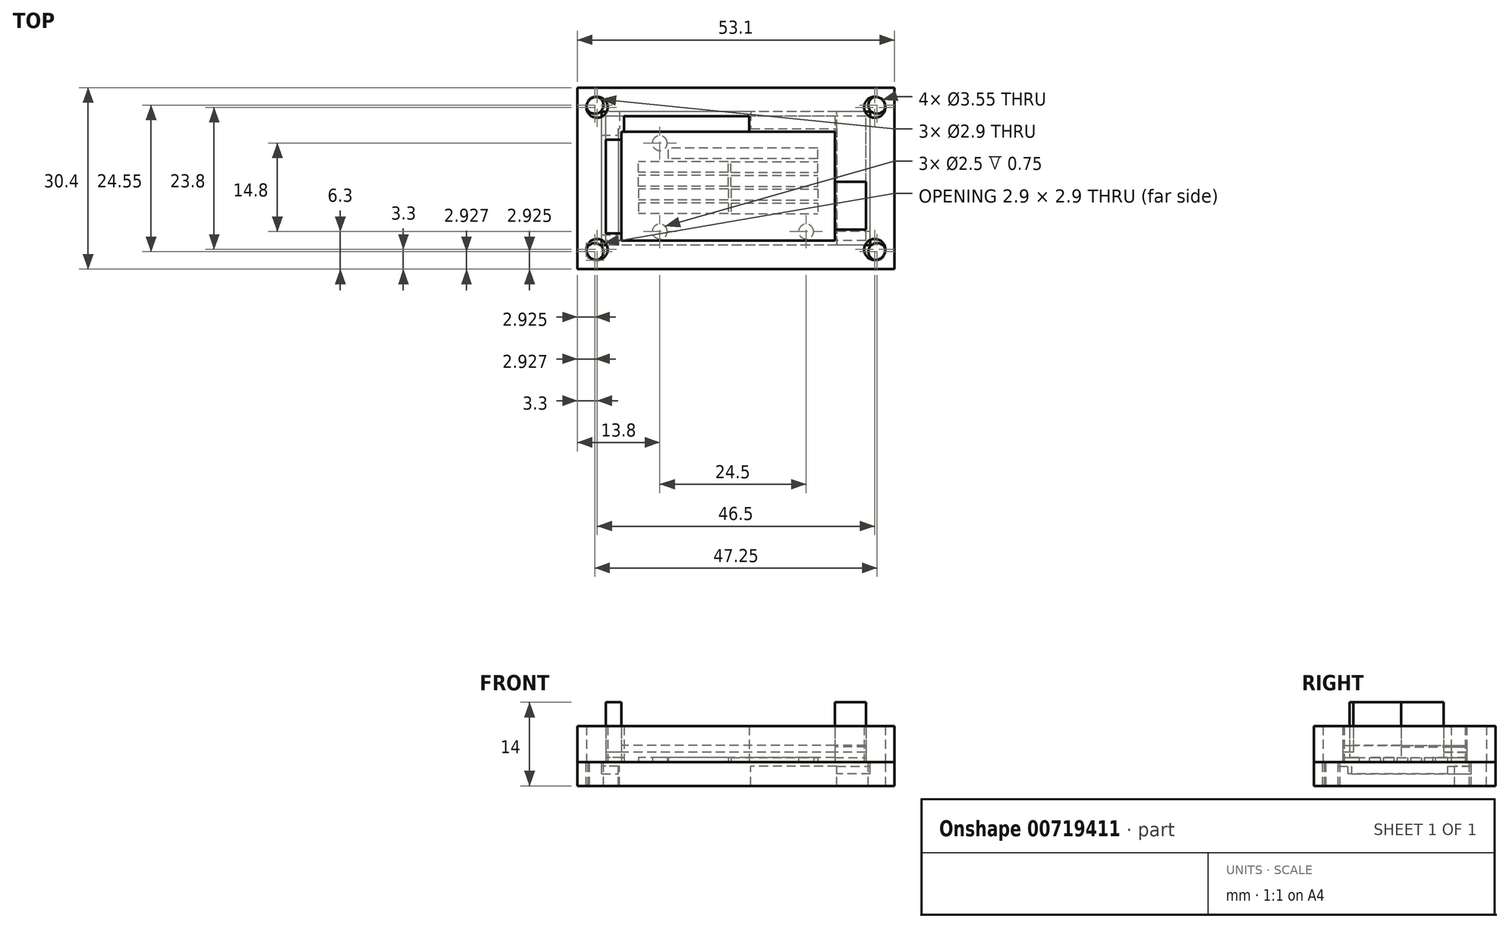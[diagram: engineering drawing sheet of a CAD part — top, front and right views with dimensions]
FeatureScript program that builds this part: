
annotation { "Feature Type Name" : "Feature", "Feature Type Description" : "" }
export const myFeature = defineFeature(function(context is Context, id is Id, definition is map)
    precondition{}
    {
        {
            var Q0;
            Q0=qCreatedBy(makeId("Top.planeOp"),FACE);
            var sketch = newSketch(context, id + "F0", { "sketchPlane" : qUnion([Q0])});
            skLineSegment(sketch, "E0.bottom", {"start": v(21.75, -10.4) * mm, "end": v(-21.75, -10.4) * mm});
            skLineSegment(sketch, "E0.top", {"start": v(21.75, 10.4) * mm, "end": v(-21.75, 10.4) * mm});
            skLineSegment(sketch, "E0.left", {"start": v(21.75, -10.4) * mm, "end": v(21.75, 10.4) * mm});
            skLineSegment(sketch, "E0.right", {"start": v(-21.75, -10.4) * mm, "end": v(-21.75, 10.4) * mm});
            skPoint(sketch, "E0.middle", {"position": v(0, 0) * mm});
            skLineSegment(sketch, "E1.bottom", {"start": v(-21.75, 6.5) * mm, "end": v(-19.15, 6.5) * mm});
            skLineSegment(sketch, "E1.top", {"start": v(-21.75, -9.2) * mm, "end": v(-19.15, -9.2) * mm});
            skLineSegment(sketch, "E1.left", {"start": v(-21.75, 6.5) * mm, "end": v(-21.75, -9.2) * mm});
            skLineSegment(sketch, "E1.right", {"start": v(-19.15, 6.5) * mm, "end": v(-19.15, -9.2) * mm});
            skLineSegment(sketch, "E2.bottom", {"start": v(-18.75, 10.4) * mm, "end": v(2.25, 10.4) * mm});
            skLineSegment(sketch, "E2.top", {"start": v(-18.75, 7.8) * mm, "end": v(2.25, 7.8) * mm});
            skLineSegment(sketch, "E2.left", {"start": v(-18.75, 10.4) * mm, "end": v(-18.75, 7.8) * mm});
            skLineSegment(sketch, "E2.right", {"start": v(2.25, 10.4) * mm, "end": v(2.25, 7.8) * mm});
            skLineSegment(sketch, "E3.bottom", {"start": v(21.75, -0.6) * mm, "end": v(16.55, -0.6) * mm});
            skLineSegment(sketch, "E3.top", {"start": v(21.75, -8.6) * mm, "end": v(16.55, -8.6) * mm});
            skLineSegment(sketch, "E3.left", {"start": v(21.75, -0.6) * mm, "end": v(21.75, -8.6) * mm});
            skLineSegment(sketch, "E3.right", {"start": v(16.55, -0.6) * mm, "end": v(16.55, -8.6) * mm});
            skCircle(sketch, "E4", {"center": v(-12.75, 5.9) * mm, "radius": 1.25 * mm});
            skCircle(sketch, "E5", {"center": v(-12.75, -8.9) * mm, "radius": 1.25 * mm});
            skCircle(sketch, "E6", {"center": v(11.75, -8.9) * mm, "radius": 1.25 * mm});
            skLineSegment(sketch, "E7.bottom", {"start": v(-19.15, -10.4) * mm, "end": v(16.55, -10.4) * mm});
            skLineSegment(sketch, "E7.top", {"start": v(-19.15, 7.8) * mm, "end": v(16.55, 7.8) * mm});
            skLineSegment(sketch, "E7.left", {"start": v(-19.15, -10.4) * mm, "end": v(-19.15, 7.8) * mm});
            skLineSegment(sketch, "E7.right", {"start": v(16.55, -10.4) * mm, "end": v(16.55, 7.8) * mm});
            skLineSegment(sketch, "E8.top", {"start": v(21.75, 10.4) * mm, "end": v(16.55, 10.4) * mm});
            skLineSegment(sketch, "E8.left", {"start": v(21.75, -0.6) * mm, "end": v(21.75, 10.4) * mm});
            skLineSegment(sketch, "E8.right", {"start": v(16.55, -0.6) * mm, "end": v(16.55, 10.4) * mm});
            skSolve(sketch);
        }
        {
            var Q0;
            Q0 = qSketchRegion(id + "F0", true);
            var Q1;
            Q1=makeQuery(id+"F0.imprint","IMPRINT",FACE,{"disambiguationData":[TD([[makeQuery(id+"F0.imprint","IMPRINT",EDGE,{"derivedFrom":sQuery(id+"F0.wireOp",EDGE,"E6")}),1.0]])]});
            var Q2;
            Q2=makeQuery(id+"F0.imprint","IMPRINT",FACE,{"disambiguationData":[TD([[makeQuery(id+"F0.imprint","IMPRINT",EDGE,{"derivedFrom":sQuery(id+"F0.wireOp",EDGE,"E5")}),1.0]])]});
            var Q3;
            Q3=makeQuery(id+"F0.imprint","IMPRINT",FACE,{"disambiguationData":[TD([[makeQuery(id+"F0.imprint","IMPRINT",EDGE,{"derivedFrom":sQuery(id+"F0.wireOp",EDGE,"E4")}),1.0]])]});
            extrude(context, id + "F1", {"entities" : qUnion([Q0, Q1, Q2, Q3]), "depth" : 1.6 * mm, "offsetDistance" : 25 * mm});
        }
        {
            var Q0;
            {var subQ0=sQuery(id+"F0.wireOp",EDGE,"E1.bottom");Q0=makeQuery(id+"F0.imprint","IMPRINT",FACE,{"disambiguationData":[TD([[makeQuery(id+"F0.imprint","IMPRINT",EDGE,{"derivedFrom":subQ0}),-1.0]])]});}
            var Q1;
            Q1=makeQuery(id+"F0.imprint","IMPRINT",FACE,{"disambiguationData":[TD([[makeQuery(id+"F0.imprint","IMPRINT",EDGE,{"derivedFrom":sQuery(id+"F0.wireOp",EDGE,"E2.bottom")}),-1.0]])]});
            var Q2;
            {var subQ0=sQuery(id+"F0.wireOp",EDGE,"E3.top");Q2=makeQuery(id+"F0.imprint","IMPRINT",FACE,{"disambiguationData":[TD([[makeQuery(id+"F0.imprint","IMPRINT",EDGE,{"derivedFrom":subQ0}),-1.0]])]});}
            extrude(context, id + "F2", {"entities" : qUnion([Q0, Q1, Q2]), "operationType" : NewBodyOperationType.ADD, "depth" : 10 * mm, "offsetDistance" : 25 * mm});
        }
        {
            var Q0;
            Q0=makeQuery(id+"F0.imprint","IMPRINT",FACE,{"disambiguationData":[TD([[makeQuery(id+"F0.imprint","IMPRINT",EDGE,{"derivedFrom":sQuery(id+"F0.wireOp",EDGE,"E4")}),-1.0]])]});
            var Q1;
            {var subQ2=sQuery(id+"F0.wireOp",EDGE,"E3.bottom");Q1=makeQuery(id+"F0.imprint","IMPRINT",FACE,{"disambiguationData":[TD([[makeQuery(id+"F0.imprint","IMPRINT",EDGE,{"derivedFrom":subQ2}),-1.0]])]});}
            var Q2;
            Q2=makeQuery(id+"F0.imprint","IMPRINT",FACE,{"disambiguationData":[TD([[makeQuery(id+"F0.imprint","IMPRINT",EDGE,{"derivedFrom":sQuery(id+"F0.wireOp",EDGE,"E4")}),1.0]])]});
            var Q3;
            Q3=makeQuery(id+"F0.imprint","IMPRINT",FACE,{"disambiguationData":[TD([[makeQuery(id+"F0.imprint","IMPRINT",EDGE,{"derivedFrom":sQuery(id+"F0.wireOp",EDGE,"E5")}),1.0]])]});
            var Q4;
            Q4=makeQuery(id+"F0.imprint","IMPRINT",FACE,{"disambiguationData":[TD([[makeQuery(id+"F0.imprint","IMPRINT",EDGE,{"derivedFrom":sQuery(id+"F0.wireOp",EDGE,"E6")}),1.0]])]});
            extrude(context, id + "F3", {"entities" : qUnion([Q0, Q1, Q2, Q3, Q4]), "operationType" : NewBodyOperationType.ADD, "depth" : 2.8 * mm, "offsetDistance" : 25 * mm});
        }
        {
            var Q0;
            Q0=qCreatedBy(makeId("Top.planeOp"),FACE);
            var sketch = newSketch(context, id + "F4", { "sketchPlane" : qUnion([Q0])});
            skLineSegment(sketch, "E9.bottom", {"start": v(26.55, -15.2) * mm, "end": v(-26.55, -15.2) * mm});
            skLineSegment(sketch, "E9.top", {"start": v(26.55, 15.2) * mm, "end": v(-26.55, 15.2) * mm});
            skLineSegment(sketch, "E9.left", {"start": v(26.55, -15.2) * mm, "end": v(26.55, 15.2) * mm});
            skLineSegment(sketch, "E9.right", {"start": v(-26.55, -15.2) * mm, "end": v(-26.55, 15.2) * mm});
            skPoint(sketch, "E9.middle", {"position": v(0, 0) * mm});
            skLineSegment(sketch, "E10.bottom", {"start": v(24.75, -13.4) * mm, "end": v(-24.75, -13.4) * mm});
            skLineSegment(sketch, "E10.top", {"start": v(24.75, 13.4) * mm, "end": v(-24.75, 13.4) * mm});
            skLineSegment(sketch, "E10.left", {"start": v(24.75, -13.4) * mm, "end": v(24.75, 13.4) * mm});
            skLineSegment(sketch, "E10.right", {"start": v(-24.75, -13.4) * mm, "end": v(-24.75, 13.4) * mm});
            skLineSegment(sketch, "E11.bottom", {"start": v(22.5, -11.15) * mm, "end": v(-22.5, -11.15) * mm});
            skLineSegment(sketch, "E11.top", {"start": v(22.5, 11.15) * mm, "end": v(-22.5, 11.15) * mm});
            skLineSegment(sketch, "E11.left", {"start": v(22.5, -11.15) * mm, "end": v(22.5, 11.15) * mm});
            skLineSegment(sketch, "E11.right", {"start": v(-22.5, -11.15) * mm, "end": v(-22.5, 11.15) * mm});
            skLineSegment(sketch, "E12.bottom", {"start": v(-22.5, 7.25) * mm, "end": v(-19.7, 7.25) * mm});
            skLineSegment(sketch, "E12.top", {"start": v(-22.5, -9.45) * mm, "end": v(-19.7, -9.45) * mm});
            skLineSegment(sketch, "E12.left", {"start": v(-22.5, 7.25) * mm, "end": v(-22.5, -9.45) * mm});
            skLineSegment(sketch, "E12.right", {"start": v(-19.7, 7.25) * mm, "end": v(-19.7, -9.45) * mm});
            skLineSegment(sketch, "E13.bottom", {"start": v(-19.5, 11.15) * mm, "end": v(2.5, 11.15) * mm});
            skLineSegment(sketch, "E13.top", {"start": v(-19.5, 8.35) * mm, "end": v(2.5, 8.35) * mm});
            skLineSegment(sketch, "E13.left", {"start": v(-19.5, 11.15) * mm, "end": v(-19.5, 8.35) * mm});
            skLineSegment(sketch, "E13.right", {"start": v(2.5, 11.15) * mm, "end": v(2.5, 8.35) * mm});
            skLineSegment(sketch, "E14.bottom", {"start": v(22.5, 0.15) * mm, "end": v(16.9, 0.15) * mm});
            skLineSegment(sketch, "E14.top", {"start": v(22.5, -8.85) * mm, "end": v(16.9, -8.85) * mm});
            skLineSegment(sketch, "E14.left", {"start": v(22.5, 0.15) * mm, "end": v(22.5, -8.85) * mm});
            skLineSegment(sketch, "E14.right", {"start": v(16.9, 0.15) * mm, "end": v(16.9, -8.85) * mm});
            skLineSegment(sketch, "E15.bottom", {"start": v(-19.7, -11.15) * mm, "end": v(16.9, -11.15) * mm});
            skLineSegment(sketch, "E15.top", {"start": v(-19.7, 8.35) * mm, "end": v(16.9, 8.35) * mm});
            skLineSegment(sketch, "E15.left", {"start": v(-19.7, -11.15) * mm, "end": v(-19.7, 8.35) * mm});
            skLineSegment(sketch, "E15.right", {"start": v(16.9, -11.15) * mm, "end": v(16.9, 8.35) * mm});
            skLineSegment(sketch, "E16.top", {"start": v(22.5, 11.15) * mm, "end": v(16.9, 11.15) * mm});
            skLineSegment(sketch, "E16.left", {"start": v(22.5, 0.15) * mm, "end": v(22.5, 11.15) * mm});
            skLineSegment(sketch, "E16.right", {"start": v(16.9, 0.15) * mm, "end": v(16.9, 11.15) * mm});
            skLineSegment(sketch, "E17", {"start": v(-22.5, 11.15) * mm, "end": v(-24.75, 13.4) * mm, "construction": true});
            skCircle(sketch, "E18", {"center": v(-23.62, 12.27) * mm, "radius": 1.45 * mm});
            skCircle(sketch, "E19", {"center": v(-23.62, 12.27) * mm, "radius": 3 * mm, "construction": true});
            skLineSegment(sketch, "E20", {"start": v(-22.5, -11.15) * mm, "end": v(-24.75, -13.4) * mm, "construction": true});
            skLineSegment(sketch, "E21", {"start": v(22.5, -11.15) * mm, "end": v(24.75, -13.4) * mm, "construction": true});
            skLineSegment(sketch, "E22", {"start": v(22.5, 11.15) * mm, "end": v(24.75, 13.4) * mm, "construction": true});
            skCircle(sketch, "E23", {"center": v(23.62, 12.28) * mm, "radius": 1.45 * mm});
            skCircle(sketch, "E24", {"center": v(23.62, -12.28) * mm, "radius": 1.45 * mm});
            skCircle(sketch, "E25", {"center": v(-23.63, -12.27) * mm, "radius": 1.45 * mm});
            skSolve(sketch);
        }
        {
            var Q0;
            {var subQ0=sQuery(id+"F4.wireOp",EDGE,"E10.left");var subQ1=sQuery(id+"F4.wireOp",EDGE,"E10.bottom");var subQ2=makeQuery(id+"F4.imprint","INTERSECT",VERTEX,{"derivedFrom":[subQ1,subQ0]});Q0=makeQuery(id+"F4.imprint","IMPRINT",FACE,{"disambiguationData":[TD([[makeQuery(id+"F4.imprint","IMPRINT",EDGE,{"disambiguationData":[TD([[subQ2,-1.0]])],"derivedFrom":subQ1}),-1.0]])]});}
            var Q1;
            Q1=makeQuery(id+"F4.imprint","IMPRINT",FACE,{"disambiguationData":[TD([[makeQuery(id+"F4.imprint","IMPRINT",EDGE,{"derivedFrom":sQuery(id+"F4.wireOp",EDGE,"E9.bottom")}),-1.0]])]});
            var Q2;
            {var subQ0=sQuery(id+"F4.wireOp",EDGE,"E14.top");Q2=makeQuery(id+"F4.imprint","IMPRINT",FACE,{"disambiguationData":[TD([[makeQuery(id+"F4.imprint","IMPRINT",EDGE,{"derivedFrom":subQ0}),-1.0]])]});}
            var Q3;
            {var subQ2=sQuery(id+"F4.wireOp",EDGE,"E14.bottom");Q3=makeQuery(id+"F4.imprint","IMPRINT",FACE,{"disambiguationData":[TD([[makeQuery(id+"F4.imprint","IMPRINT",EDGE,{"derivedFrom":subQ2}),-1.0]])]});}
            var Q4;
            Q4=makeQuery(id+"F4.imprint","IMPRINT",FACE,{"disambiguationData":[TD([[makeQuery(id+"F4.imprint","IMPRINT",EDGE,{"derivedFrom":sQuery(id+"F4.wireOp",EDGE,"E13.bottom")}),-1.0]])]});
            var Q5;
            {var subQ0=sQuery(id+"F4.wireOp",EDGE,"E12.bottom");Q5=makeQuery(id+"F4.imprint","IMPRINT",FACE,{"disambiguationData":[TD([[makeQuery(id+"F4.imprint","IMPRINT",EDGE,{"derivedFrom":subQ0}),-1.0]])]});}
            var Q6;
            {var subQ0=sQuery(id+"F4.wireOp",EDGE,"E12.bottom");Q6=makeQuery(id+"F4.imprint","IMPRINT",FACE,{"disambiguationData":[TD([[makeQuery(id+"F4.imprint","IMPRINT",EDGE,{"derivedFrom":subQ0}),1.0]])]});}
            var Q7;
            {var subQ3=sQuery(id+"F4.wireOp",EDGE,"E13.right");Q7=makeQuery(id+"F4.imprint","IMPRINT",FACE,{"disambiguationData":[TD([[makeQuery(id+"F4.imprint","IMPRINT",EDGE,{"derivedFrom":subQ3}),1.0]])]});}
            var Q8;
            {var subQ5=sQuery(id+"F4.wireOp",EDGE,"E12.top");Q8=makeQuery(id+"F4.imprint","IMPRINT",FACE,{"disambiguationData":[TD([[makeQuery(id+"F4.imprint","IMPRINT",EDGE,{"derivedFrom":subQ5}),-1.0]])]});}
            var Q9;
            {var subQ0=sQuery(id+"F4.wireOp",EDGE,"E11.left");Q9=makeQuery(id+"F4.imprint","IMPRINT",FACE,{"disambiguationData":[TD([[makeQuery(id+"F4.imprint","IMPRINT",EDGE,{"derivedFrom":subQ0}),1.0]])]});}
            var Q10;
            {var subQ9=sQuery(id+"F4.wireOp",EDGE,"E15.bottom");Q10=makeQuery(id+"F4.imprint","IMPRINT",FACE,{"disambiguationData":[TD([[makeQuery(id+"F4.imprint","IMPRINT",EDGE,{"derivedFrom":subQ9}),1.0]])]});}
            var Q11;
            {var subQ13=sQuery(id+"F4.wireOp",EDGE,"E11.left");Q11=makeQuery(id+"F4.imprint","IMPRINT",FACE,{"disambiguationData":[TD([[makeQuery(id+"F4.imprint","IMPRINT",EDGE,{"derivedFrom":subQ13}),-1.0]])]});}
            var Q12;
            {var subQ0=sQuery(id+"F4.wireOp",EDGE,"E10.left");var subQ1=sQuery(id+"F4.wireOp",EDGE,"E10.top");var subQ2=makeQuery(id+"F4.imprint","INTERSECT",VERTEX,{"derivedFrom":[subQ1,subQ0]});Q12=makeQuery(id+"F4.imprint","IMPRINT",FACE,{"disambiguationData":[TD([[makeQuery(id+"F4.imprint","IMPRINT",EDGE,{"disambiguationData":[TD([[subQ2,-1.0]])],"derivedFrom":subQ1}),1.0]])]});}
            var Q13;
            {var subQ0=sQuery(id+"F4.wireOp",EDGE,"E10.right");var subQ1=sQuery(id+"F4.wireOp",EDGE,"E10.top");var subQ2=makeQuery(id+"F4.imprint","INTERSECT",VERTEX,{"derivedFrom":[subQ1,subQ0]});Q13=makeQuery(id+"F4.imprint","IMPRINT",FACE,{"disambiguationData":[TD([[makeQuery(id+"F4.imprint","IMPRINT",EDGE,{"disambiguationData":[TD([[subQ2,1.0]])],"derivedFrom":subQ1}),1.0]])]});}
            extrude(context, id + "F5", {"entities" : qUnion([Q0, Q1, Q2, Q3, Q4, Q5, Q6, Q7, Q8, Q9, Q10, Q11, Q12, Q13]), "oppositeDirection" : true, "depth" : 4 * mm, "offsetDistance" : 25 * mm});
        }
        {
            var Q0;
            Q0=makeQuery(id+"F4.imprint","IMPRINT",FACE,{"disambiguationData":[TD([[makeQuery(id+"F4.imprint","IMPRINT",EDGE,{"derivedFrom":sQuery(id+"F4.wireOp",EDGE,"E13.bottom")}),-1.0]])]});
            var Q1;
            {var subQ9=sQuery(id+"F4.wireOp",EDGE,"E15.bottom");Q1=makeQuery(id+"F4.imprint","IMPRINT",FACE,{"disambiguationData":[TD([[makeQuery(id+"F4.imprint","IMPRINT",EDGE,{"derivedFrom":subQ9}),1.0]])]});}
            var Q2;
            {var subQ0=sQuery(id+"F4.wireOp",EDGE,"E12.bottom");Q2=makeQuery(id+"F4.imprint","IMPRINT",FACE,{"disambiguationData":[TD([[makeQuery(id+"F4.imprint","IMPRINT",EDGE,{"derivedFrom":subQ0}),-1.0]])]});}
            var Q3;
            {var subQ2=sQuery(id+"F4.wireOp",EDGE,"E14.bottom");Q3=makeQuery(id+"F4.imprint","IMPRINT",FACE,{"disambiguationData":[TD([[makeQuery(id+"F4.imprint","IMPRINT",EDGE,{"derivedFrom":subQ2}),-1.0]])]});}
            var Q4;
            {var subQ0=sQuery(id+"F4.wireOp",EDGE,"E14.top");Q4=makeQuery(id+"F4.imprint","IMPRINT",FACE,{"disambiguationData":[TD([[makeQuery(id+"F4.imprint","IMPRINT",EDGE,{"derivedFrom":subQ0}),-1.0]])]});}
            extrude(context, id + "F6", {"entities" : qUnion([Q0, Q1, Q2, Q3, Q4]), "operationType" : NewBodyOperationType.REMOVE, "oppositeDirection" : true, "depth" : 2 * mm, "offsetDistance" : 25 * mm});
        }
        {
            var Q0;
            {var subQ0=sQuery(id+"F4.wireOp",EDGE,"E12.bottom");Q0=makeQuery(id+"F4.imprint","IMPRINT",FACE,{"disambiguationData":[TD([[makeQuery(id+"F4.imprint","IMPRINT",EDGE,{"derivedFrom":subQ0}),1.0]])]});}
            var Q1;
            {var subQ5=sQuery(id+"F4.wireOp",EDGE,"E12.top");Q1=makeQuery(id+"F4.imprint","IMPRINT",FACE,{"disambiguationData":[TD([[makeQuery(id+"F4.imprint","IMPRINT",EDGE,{"derivedFrom":subQ5}),-1.0]])]});}
            var Q2;
            {var subQ0=sQuery(id+"F4.wireOp",EDGE,"E11.left");Q2=makeQuery(id+"F4.imprint","IMPRINT",FACE,{"disambiguationData":[TD([[makeQuery(id+"F4.imprint","IMPRINT",EDGE,{"derivedFrom":subQ0}),1.0]])]});}
            var Q3;
            {var subQ3=sQuery(id+"F4.wireOp",EDGE,"E13.right");Q3=makeQuery(id+"F4.imprint","IMPRINT",FACE,{"disambiguationData":[TD([[makeQuery(id+"F4.imprint","IMPRINT",EDGE,{"derivedFrom":subQ3}),1.0]])]});}
            extrude(context, id + "F7", {"entities" : qUnion([Q0, Q1, Q2, Q3]), "operationType" : NewBodyOperationType.REMOVE, "oppositeDirection" : true, "depth" : 0.75 * mm, "offsetDistance" : 25 * mm});
        }
        {
            var Q0;
            Q0=qCreatedBy(makeId("Top.planeOp"),FACE);
            var sketch = newSketch(context, id + "F8", { "sketchPlane" : qUnion([Q0])});
            skLineSegment(sketch, "E26.bottom", {"start": v(26.55, -15.2) * mm, "end": v(-26.55, -15.2) * mm});
            skLineSegment(sketch, "E26.top", {"start": v(26.55, 15.2) * mm, "end": v(-26.55, 15.2) * mm});
            skLineSegment(sketch, "E26.left", {"start": v(26.55, -15.2) * mm, "end": v(26.55, 15.2) * mm});
            skLineSegment(sketch, "E26.right", {"start": v(-26.55, -15.2) * mm, "end": v(-26.55, 15.2) * mm});
            skLineSegment(sketch, "E27.bottom", {"start": v(24.75, -13.4) * mm, "end": v(-24.75, -13.4) * mm});
            skLineSegment(sketch, "E27.top", {"start": v(24.75, 13.4) * mm, "end": v(-24.75, 13.4) * mm});
            skLineSegment(sketch, "E27.left", {"start": v(24.75, -13.4) * mm, "end": v(24.75, 13.4) * mm});
            skLineSegment(sketch, "E27.right", {"start": v(-24.75, -13.4) * mm, "end": v(-24.75, 13.4) * mm});
            skLineSegment(sketch, "E28.bottom", {"start": v(21.75, -10.4) * mm, "end": v(-21.75, -10.4) * mm});
            skLineSegment(sketch, "E28.top", {"start": v(21.75, 10.4) * mm, "end": v(-21.75, 10.4) * mm});
            skLineSegment(sketch, "E28.left", {"start": v(21.75, -10.4) * mm, "end": v(21.75, 10.4) * mm});
            skLineSegment(sketch, "E28.right", {"start": v(-21.75, -10.4) * mm, "end": v(-21.75, 10.4) * mm});
            skLineSegment(sketch, "E29.bottom", {"start": v(-21.75, 6.5) * mm, "end": v(-19.15, 6.5) * mm});
            skLineSegment(sketch, "E29.top", {"start": v(-21.75, -9.2) * mm, "end": v(-19.15, -9.2) * mm});
            skLineSegment(sketch, "E29.left", {"start": v(-21.75, 6.5) * mm, "end": v(-21.75, -9.2) * mm});
            skLineSegment(sketch, "E29.right", {"start": v(-19.15, 6.5) * mm, "end": v(-19.15, -9.2) * mm});
            skLineSegment(sketch, "E30.bottom", {"start": v(-18.75, 10.4) * mm, "end": v(2.25, 10.4) * mm});
            skLineSegment(sketch, "E30.top", {"start": v(-18.75, 7.8) * mm, "end": v(2.25, 7.8) * mm});
            skLineSegment(sketch, "E30.left", {"start": v(-18.75, 10.4) * mm, "end": v(-18.75, 7.8) * mm});
            skLineSegment(sketch, "E30.right", {"start": v(2.25, 10.4) * mm, "end": v(2.25, 7.8) * mm});
            skLineSegment(sketch, "E31.bottom", {"start": v(21.75, -0.6) * mm, "end": v(16.55, -0.6) * mm});
            skLineSegment(sketch, "E31.top", {"start": v(21.75, -8.6) * mm, "end": v(16.55, -8.6) * mm});
            skLineSegment(sketch, "E31.left", {"start": v(21.75, -0.6) * mm, "end": v(21.75, -8.6) * mm});
            skLineSegment(sketch, "E31.right", {"start": v(16.55, -0.6) * mm, "end": v(16.55, -8.6) * mm});
            skLineSegment(sketch, "E32.bottom", {"start": v(-19.15, -10.4) * mm, "end": v(16.55, -10.4) * mm});
            skLineSegment(sketch, "E32.top", {"start": v(-19.15, 7.8) * mm, "end": v(16.55, 7.8) * mm});
            skLineSegment(sketch, "E32.left", {"start": v(-19.15, -10.4) * mm, "end": v(-19.15, 7.8) * mm});
            skLineSegment(sketch, "E32.right", {"start": v(16.55, -10.4) * mm, "end": v(16.55, 7.8) * mm});
            skLineSegment(sketch, "E33.top", {"start": v(21.75, 10.4) * mm, "end": v(16.55, 10.4) * mm});
            skLineSegment(sketch, "E33.left", {"start": v(21.75, -0.6) * mm, "end": v(21.75, 10.4) * mm});
            skLineSegment(sketch, "E33.right", {"start": v(16.55, -0.6) * mm, "end": v(16.55, 10.4) * mm});
            skLineSegment(sketch, "E34", {"start": v(-21.75, 10.4) * mm, "end": v(-24.75, 13.4) * mm, "construction": true});
            skCircle(sketch, "E35", {"center": v(-23.25, 11.9) * mm, "radius": 1.77 * mm});
            skCircle(sketch, "E36", {"center": v(-23.25, 11.9) * mm, "radius": 3 * mm, "construction": true});
            skLineSegment(sketch, "E37", {"start": v(-21.75, -10.4) * mm, "end": v(-24.75, -13.4) * mm, "construction": true});
            skLineSegment(sketch, "E38", {"start": v(21.75, -10.4) * mm, "end": v(24.75, -13.4) * mm, "construction": true});
            skLineSegment(sketch, "E39", {"start": v(21.75, 10.4) * mm, "end": v(24.75, 13.4) * mm, "construction": true});
            skCircle(sketch, "E40", {"center": v(23.25, 11.9) * mm, "radius": 1.77 * mm});
            skCircle(sketch, "E41", {"center": v(23.25, -11.9) * mm, "radius": 1.77 * mm});
            skCircle(sketch, "E42", {"center": v(-23.25, -11.9) * mm, "radius": 1.77 * mm});
            skCircle(sketch, "E43", {"center": v(-12.75, 5.9) * mm, "radius": 1.25 * mm});
            skCircle(sketch, "E44", {"center": v(-12.75, -8.9) * mm, "radius": 1.25 * mm});
            skCircle(sketch, "E45", {"center": v(11.75, -8.9) * mm, "radius": 1.25 * mm});
            skLineSegment(sketch, "E46", {"start": v(-19.15, -1.3) * mm, "end": v(16.55, -1.3) * mm, "construction": true});
            skLineSegment(sketch, "E47", {"start": v(-1.3, 7.8) * mm, "end": v(-1.3, -10.4) * mm, "construction": true});
            skPoint(sketch, "E48", {"position": v(-1.3, -1.3) * mm});
            skLineSegment(sketch, "E49.bottom", {"start": v(-1.3, -1.3) * mm, "end": v(-16.3, -1.3) * mm});
            skLineSegment(sketch, "E49.top", {"start": v(-1.3, 0.5) * mm, "end": v(-16.3, 0.5) * mm});
            skLineSegment(sketch, "E49.left", {"start": v(-1.3, -1.3) * mm, "end": v(-1.3, 0.5) * mm});
            skLineSegment(sketch, "E49.right", {"start": v(-16.3, -1.3) * mm, "end": v(-16.3, 0.5) * mm});
            skLineSegment(sketch, "E50.bottom", {"start": v(-1.3, -1.8) * mm, "end": v(-16.3, -1.8) * mm});
            skLineSegment(sketch, "E50.top", {"start": v(-1.3, -3.6) * mm, "end": v(-16.3, -3.6) * mm});
            skLineSegment(sketch, "E50.left", {"start": v(-1.3, -1.8) * mm, "end": v(-1.3, -3.6) * mm});
            skLineSegment(sketch, "E50.right", {"start": v(-16.3, -1.8) * mm, "end": v(-16.3, -3.6) * mm});
            skLineSegment(sketch, "E51.bottom", {"start": v(-1.3, 1) * mm, "end": v(-16.3, 1) * mm});
            skLineSegment(sketch, "E51.top", {"start": v(-1.3, 2.8) * mm, "end": v(-16.3, 2.8) * mm});
            skLineSegment(sketch, "E51.left", {"start": v(-1.3, 1) * mm, "end": v(-1.3, 2.8) * mm});
            skLineSegment(sketch, "E51.right", {"start": v(-16.3, 1) * mm, "end": v(-16.3, 2.8) * mm});
            skLineSegment(sketch, "E52.bottom", {"start": v(-1.3, -4.1) * mm, "end": v(-16.3, -4.1) * mm});
            skLineSegment(sketch, "E52.top", {"start": v(-1.3, -5.9) * mm, "end": v(-16.3, -5.9) * mm});
            skLineSegment(sketch, "E52.left", {"start": v(-1.3, -4.1) * mm, "end": v(-1.3, -5.9) * mm});
            skLineSegment(sketch, "E52.right", {"start": v(-16.3, -4.1) * mm, "end": v(-16.3, -5.9) * mm});
            skLineSegment(sketch, "E53", {"start": v(-0.8, 6.5) * mm, "end": v(-0.8, -7.96) * mm, "construction": true});
            skLineSegment(sketch, "E54.bottom", {"start": v(-0.8, -1.3) * mm, "end": v(13.7, -1.3) * mm});
            skLineSegment(sketch, "E54.top", {"start": v(-0.8, 0.5) * mm, "end": v(13.7, 0.5) * mm});
            skLineSegment(sketch, "E54.left", {"start": v(-0.8, -1.3) * mm, "end": v(-0.8, 0.5) * mm});
            skLineSegment(sketch, "E54.right", {"start": v(13.7, -1.3) * mm, "end": v(13.7, 0.5) * mm});
            skLineSegment(sketch, "E55.bottom", {"start": v(-0.8, 1) * mm, "end": v(13.7, 1) * mm});
            skLineSegment(sketch, "E55.top", {"start": v(-0.8, 2.8) * mm, "end": v(13.7, 2.8) * mm});
            skLineSegment(sketch, "E55.left", {"start": v(-0.8, 1) * mm, "end": v(-0.8, 2.8) * mm});
            skLineSegment(sketch, "E55.right", {"start": v(13.7, 1) * mm, "end": v(13.7, 2.8) * mm});
            skLineSegment(sketch, "E56.bottom", {"start": v(-0.8, -1.8) * mm, "end": v(13.7, -1.8) * mm});
            skLineSegment(sketch, "E56.top", {"start": v(-0.8, -3.6) * mm, "end": v(13.7, -3.6) * mm});
            skLineSegment(sketch, "E56.left", {"start": v(-0.8, -1.8) * mm, "end": v(-0.8, -3.6) * mm});
            skLineSegment(sketch, "E56.right", {"start": v(13.7, -1.8) * mm, "end": v(13.7, -3.6) * mm});
            skLineSegment(sketch, "E57.bottom", {"start": v(-0.8, -4.1) * mm, "end": v(13.7, -4.1) * mm});
            skLineSegment(sketch, "E57.top", {"start": v(-0.8, -5.9) * mm, "end": v(13.7, -5.9) * mm});
            skLineSegment(sketch, "E57.left", {"start": v(-0.8, -4.1) * mm, "end": v(-0.8, -5.9) * mm});
            skLineSegment(sketch, "E57.right", {"start": v(13.7, -4.1) * mm, "end": v(13.7, -5.9) * mm});
            skLineSegment(sketch, "E58.bottom", {"start": v(13.7, 3.3) * mm, "end": v(-11.3, 3.3) * mm});
            skLineSegment(sketch, "E58.top", {"start": v(13.7, 5.1) * mm, "end": v(-11.3, 5.1) * mm});
            skLineSegment(sketch, "E58.left", {"start": v(13.7, 3.3) * mm, "end": v(13.7, 5.1) * mm});
            skLineSegment(sketch, "E58.right", {"start": v(-11.3, 3.3) * mm, "end": v(-11.3, 5.1) * mm});
            skSolve(sketch);
        }
        {
            var Q0;
            {var subQ2=sQuery(id+"F8.wireOp",EDGE,"E31.bottom");Q0=makeQuery(id+"F8.imprint","IMPRINT",FACE,{"disambiguationData":[TD([[makeQuery(id+"F8.imprint","IMPRINT",EDGE,{"derivedFrom":subQ2}),-1.0]])]});}
            var Q1;
            {var subQ3=sQuery(id+"F8.wireOp",EDGE,"E30.right");Q1=makeQuery(id+"F8.imprint","IMPRINT",FACE,{"disambiguationData":[TD([[makeQuery(id+"F8.imprint","IMPRINT",EDGE,{"derivedFrom":subQ3}),1.0]])]});}
            var Q2;
            {var subQ0=sQuery(id+"F8.wireOp",EDGE,"E28.left");Q2=makeQuery(id+"F8.imprint","IMPRINT",FACE,{"disambiguationData":[TD([[makeQuery(id+"F8.imprint","IMPRINT",EDGE,{"derivedFrom":subQ0}),1.0]])]});}
            var Q3;
            {var subQ9=sQuery(id+"F8.wireOp",EDGE,"E32.bottom");Q3=makeQuery(id+"F8.imprint","IMPRINT",FACE,{"disambiguationData":[TD([[makeQuery(id+"F8.imprint","IMPRINT",EDGE,{"derivedFrom":subQ9}),1.0]])]});}
            var Q4;
            {var subQ0=sQuery(id+"F8.wireOp",EDGE,"E29.bottom");Q4=makeQuery(id+"F8.imprint","IMPRINT",FACE,{"disambiguationData":[TD([[makeQuery(id+"F8.imprint","IMPRINT",EDGE,{"derivedFrom":subQ0}),1.0]])]});}
            var Q5;
            {var subQ5=sQuery(id+"F8.wireOp",EDGE,"E29.top");Q5=makeQuery(id+"F8.imprint","IMPRINT",FACE,{"disambiguationData":[TD([[makeQuery(id+"F8.imprint","IMPRINT",EDGE,{"derivedFrom":subQ5}),-1.0]])]});}
            var Q6;
            {var subQ13=sQuery(id+"F8.wireOp",EDGE,"E28.left");Q6=makeQuery(id+"F8.imprint","IMPRINT",FACE,{"disambiguationData":[TD([[makeQuery(id+"F8.imprint","IMPRINT",EDGE,{"derivedFrom":subQ13}),-1.0]])]});}
            var Q7;
            Q7=makeQuery(id+"F8.imprint","IMPRINT",FACE,{"disambiguationData":[TD([[makeQuery(id+"F8.imprint","IMPRINT",EDGE,{"derivedFrom":sQuery(id+"F8.wireOp",EDGE,"E26.bottom")}),-1.0]])]});
            var Q8;
            {var subQ0=sQuery(id+"F8.wireOp",EDGE,"E27.right");var subQ1=sQuery(id+"F8.wireOp",EDGE,"E27.top");var subQ2=makeQuery(id+"F8.imprint","INTERSECT",VERTEX,{"derivedFrom":[subQ1,subQ0]});Q8=makeQuery(id+"F8.imprint","IMPRINT",FACE,{"disambiguationData":[TD([[makeQuery(id+"F8.imprint","IMPRINT",EDGE,{"disambiguationData":[TD([[subQ2,1.0]])],"derivedFrom":subQ1}),1.0]])]});}
            var Q9;
            {var subQ0=sQuery(id+"F8.wireOp",EDGE,"E27.right");var subQ1=sQuery(id+"F8.wireOp",EDGE,"E27.bottom");var subQ2=makeQuery(id+"F8.imprint","INTERSECT",VERTEX,{"derivedFrom":[subQ1,subQ0]});Q9=makeQuery(id+"F8.imprint","IMPRINT",FACE,{"disambiguationData":[TD([[makeQuery(id+"F8.imprint","IMPRINT",EDGE,{"disambiguationData":[TD([[subQ2,1.0]])],"derivedFrom":subQ1}),-1.0]])]});}
            var Q10;
            {var subQ0=sQuery(id+"F8.wireOp",EDGE,"E27.left");var subQ1=sQuery(id+"F8.wireOp",EDGE,"E27.bottom");var subQ2=makeQuery(id+"F8.imprint","INTERSECT",VERTEX,{"derivedFrom":[subQ1,subQ0]});Q10=makeQuery(id+"F8.imprint","IMPRINT",FACE,{"disambiguationData":[TD([[makeQuery(id+"F8.imprint","IMPRINT",EDGE,{"disambiguationData":[TD([[subQ2,-1.0]])],"derivedFrom":subQ1}),-1.0]])]});}
            var Q11;
            {var subQ0=sQuery(id+"F8.wireOp",EDGE,"E27.left");var subQ1=sQuery(id+"F8.wireOp",EDGE,"E27.top");var subQ2=makeQuery(id+"F8.imprint","INTERSECT",VERTEX,{"derivedFrom":[subQ1,subQ0]});Q11=makeQuery(id+"F8.imprint","IMPRINT",FACE,{"disambiguationData":[TD([[makeQuery(id+"F8.imprint","IMPRINT",EDGE,{"disambiguationData":[TD([[subQ2,-1.0]])],"derivedFrom":subQ1}),1.0]])]});}
            extrude(context, id + "F9", {"entities" : qUnion([Q0, Q1, Q2, Q3, Q4, Q5, Q6, Q7, Q8, Q9, Q10, Q11]), "depth" : 6 * mm, "offsetDistance" : 25 * mm});
        }
        {
            var Q0;
            Q0=makeQuery(id+"F8.imprint","IMPRINT",FACE,{"disambiguationData":[TD([[makeQuery(id+"F8.imprint","IMPRINT",EDGE,{"derivedFrom":sQuery(id+"F8.wireOp",EDGE,"E51.bottom")}),-1.0]])]});
            var Q1;
            Q1=makeQuery(id+"F8.imprint","IMPRINT",FACE,{"disambiguationData":[TD([[makeQuery(id+"F8.imprint","IMPRINT",EDGE,{"derivedFrom":sQuery(id+"F8.wireOp",EDGE,"E50.bottom")}),1.0]])]});
            var Q2;
            Q2=makeQuery(id+"F8.imprint","IMPRINT",FACE,{"disambiguationData":[TD([[makeQuery(id+"F8.imprint","IMPRINT",EDGE,{"derivedFrom":sQuery(id+"F8.wireOp",EDGE,"E54.bottom")}),1.0]])]});
            var Q3;
            Q3=makeQuery(id+"F8.imprint","IMPRINT",FACE,{"disambiguationData":[TD([[makeQuery(id+"F8.imprint","IMPRINT",EDGE,{"derivedFrom":sQuery(id+"F8.wireOp",EDGE,"E52.bottom")}),1.0]])]});
            var Q4;
            Q4=makeQuery(id+"F8.imprint","IMPRINT",FACE,{"disambiguationData":[TD([[makeQuery(id+"F8.imprint","IMPRINT",EDGE,{"derivedFrom":sQuery(id+"F8.wireOp",EDGE,"E58.bottom")}),-1.0]])]});
            var Q5;
            {var subQ0=sQuery(id+"F8.wireOp",EDGE,"E28.left");Q5=makeQuery(id+"F8.imprint","IMPRINT",FACE,{"disambiguationData":[TD([[makeQuery(id+"F8.imprint","IMPRINT",EDGE,{"derivedFrom":subQ0}),1.0]])]});}
            var Q6;
            {var subQ4=sQuery(id+"F8.wireOp",EDGE,"E32.bottom");Q6=makeQuery(id+"F8.imprint","IMPRINT",FACE,{"disambiguationData":[TD([[makeQuery(id+"F8.imprint","IMPRINT",EDGE,{"derivedFrom":subQ4}),1.0]])]});}
            var Q7;
            {var subQ0=sQuery(id+"F8.wireOp",EDGE,"E29.bottom");Q7=makeQuery(id+"F8.imprint","IMPRINT",FACE,{"disambiguationData":[TD([[makeQuery(id+"F8.imprint","IMPRINT",EDGE,{"derivedFrom":subQ0}),1.0]])]});}
            var Q8;
            Q8=makeQuery(id+"F8.imprint","IMPRINT",FACE,{"disambiguationData":[TD([[makeQuery(id+"F8.imprint","IMPRINT",EDGE,{"derivedFrom":sQuery(id+"F8.wireOp",EDGE,"E30.bottom")}),-1.0]])]});
            var Q9;
            {var subQ2=sQuery(id+"F8.wireOp",EDGE,"E31.bottom");Q9=makeQuery(id+"F8.imprint","IMPRINT",FACE,{"disambiguationData":[TD([[makeQuery(id+"F8.imprint","IMPRINT",EDGE,{"derivedFrom":subQ2}),-1.0]])]});}
            var Q10;
            {var subQ3=sQuery(id+"F8.wireOp",EDGE,"E30.right");Q10=makeQuery(id+"F8.imprint","IMPRINT",FACE,{"disambiguationData":[TD([[makeQuery(id+"F8.imprint","IMPRINT",EDGE,{"derivedFrom":subQ3}),1.0]])]});}
            var Q11;
            Q11=makeQuery(id+"F8.imprint","IMPRINT",FACE,{"disambiguationData":[TD([[makeQuery(id+"F8.imprint","IMPRINT",EDGE,{"derivedFrom":sQuery(id+"F8.wireOp",EDGE,"E43")}),1.0]])]});
            var Q12;
            Q12=makeQuery(id+"F8.imprint","IMPRINT",FACE,{"disambiguationData":[TD([[makeQuery(id+"F8.imprint","IMPRINT",EDGE,{"derivedFrom":sQuery(id+"F8.wireOp",EDGE,"E49.bottom")}),-1.0]])]});
            var Q13;
            Q13=makeQuery(id+"F8.imprint","IMPRINT",FACE,{"disambiguationData":[TD([[makeQuery(id+"F8.imprint","IMPRINT",EDGE,{"derivedFrom":sQuery(id+"F8.wireOp",EDGE,"E45")}),1.0]])]});
            var Q14;
            Q14=makeQuery(id+"F8.imprint","IMPRINT",FACE,{"disambiguationData":[TD([[makeQuery(id+"F8.imprint","IMPRINT",EDGE,{"derivedFrom":sQuery(id+"F8.wireOp",EDGE,"E44")}),1.0]])]});
            var Q15;
            Q15=makeQuery(id+"F8.imprint","IMPRINT",FACE,{"disambiguationData":[TD([[makeQuery(id+"F8.imprint","IMPRINT",EDGE,{"derivedFrom":sQuery(id+"F8.wireOp",EDGE,"E56.bottom")}),-1.0]])]});
            var Q16;
            {var subQ0=sQuery(id+"F8.wireOp",EDGE,"E31.top");Q16=makeQuery(id+"F8.imprint","IMPRINT",FACE,{"disambiguationData":[TD([[makeQuery(id+"F8.imprint","IMPRINT",EDGE,{"derivedFrom":subQ0}),-1.0]])]});}
            var Q17;
            Q17=makeQuery(id+"F8.imprint","IMPRINT",FACE,{"disambiguationData":[TD([[makeQuery(id+"F8.imprint","IMPRINT",EDGE,{"derivedFrom":sQuery(id+"F8.wireOp",EDGE,"E55.bottom")}),1.0]])]});
            var Q18;
            Q18=makeQuery(id+"F8.imprint","IMPRINT",FACE,{"disambiguationData":[TD([[makeQuery(id+"F8.imprint","IMPRINT",EDGE,{"derivedFrom":sQuery(id+"F8.wireOp",EDGE,"E57.bottom")}),-1.0]])]});
            var Q19;
            {var subQ5=sQuery(id+"F8.wireOp",EDGE,"E29.top");Q19=makeQuery(id+"F8.imprint","IMPRINT",FACE,{"disambiguationData":[TD([[makeQuery(id+"F8.imprint","IMPRINT",EDGE,{"derivedFrom":subQ5}),-1.0]])]});}
            var Q20;
            {var subQ0=sQuery(id+"F8.wireOp",EDGE,"E29.bottom");Q20=makeQuery(id+"F8.imprint","IMPRINT",FACE,{"disambiguationData":[TD([[makeQuery(id+"F8.imprint","IMPRINT",EDGE,{"derivedFrom":subQ0}),-1.0]])]});}
            extrude(context, id + "F10", {"entities" : qUnion([Q0, Q1, Q2, Q3, Q4, Q5, Q6, Q7, Q8, Q9, Q10, Q11, Q12, Q13, Q14, Q15, Q16, Q17, Q18, Q19, Q20]), "operationType" : NewBodyOperationType.REMOVE, "depth" : 0.75 * mm, "offsetDistance" : 25 * mm});
        }
        {
            var Q0;
            {var subQ4=sQuery(id+"F8.wireOp",EDGE,"E32.bottom");Q0=makeQuery(id+"F8.imprint","IMPRINT",FACE,{"disambiguationData":[TD([[makeQuery(id+"F8.imprint","IMPRINT",EDGE,{"derivedFrom":subQ4}),1.0]])]});}
            var Q1;
            {var subQ2=sQuery(id+"F8.wireOp",EDGE,"E31.bottom");Q1=makeQuery(id+"F8.imprint","IMPRINT",FACE,{"disambiguationData":[TD([[makeQuery(id+"F8.imprint","IMPRINT",EDGE,{"derivedFrom":subQ2}),-1.0]])]});}
            extrude(context, id + "F11", {"entities" : qUnion([Q0, Q1]), "operationType" : NewBodyOperationType.REMOVE, "depth" : 2.5 * mm, "offsetDistance" : 25 * mm});
        }
    });
